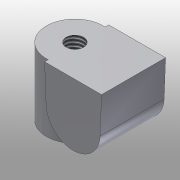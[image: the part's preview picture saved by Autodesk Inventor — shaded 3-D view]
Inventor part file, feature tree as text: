
AUTODESK INVENTOR PART (.ipt)
format: ipt  version: 2016 (Build 200138000, 138)  size: 115,712 bytes
history: native  units: mm
features: extrude x2, hole x2, sketch x2
ambient origin geometry x8: Origin, YZ Plane, XZ Plane, XY Plane, X Axis, Y Axis, Z Axis, Center Point
bodies: Solid1 (feature_tree)
feature tree (6):
  extrude  "Extrusion1"  Depth=5.0mm
  extrude  "Extrusion2"  Depth=4.0mm TaperAngle=0.0deg
  hole  "Hole1"  [1 undecoded]
  hole  "Hole2"  [1 undecoded]
  sketch  "Sketch1"  dims[d0=3.8mm d1=5.0mm]
  sketch  "Sketch2"  dims[d2=8.0mm d3=9.0mm d4=0.0mm d5=8.0mm d6=4.25mm d7=9.5mm d8=0.0mm d9=10.0mm d10=10.0mm d11=3.0mm d12=6.0mm d13=4.0mm d14=2.0mm d15=90.0deg d16=6.0mm d17=0.0mm d18=10.0mm d19=10.0mm d20=2.459mm d21=6.0mm d22=4.0mm d23=2.0mm d24=90.0deg d25=12.05mm d26=0.0mm]
note: 2 required parameter values undecoded (feature->parameter linkage not recoverable at this tier; creation-order binding heuristic only, values carry confidence <= 0.55)
